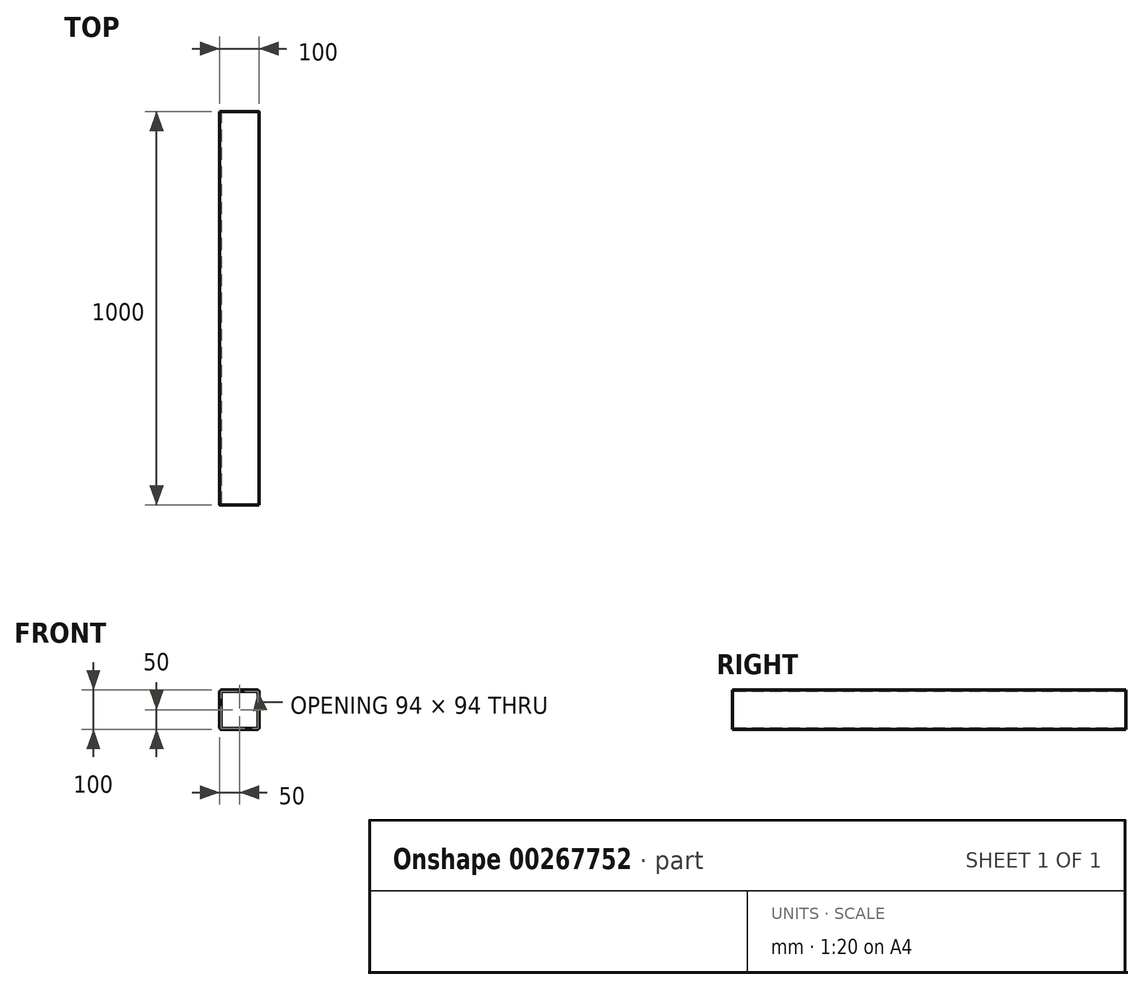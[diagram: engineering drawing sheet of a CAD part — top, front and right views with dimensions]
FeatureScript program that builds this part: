
annotation { "Feature Type Name" : "Feature", "Feature Type Description" : "" }
export const myFeature = defineFeature(function(context is Context, id is Id, definition is map)
    precondition{}
    {
        {
            var Q0;
            Q0=qCreatedBy(makeId("Front.planeOp"),FACE);
            var sketch = newSketch(context, id + "F0", { "sketchPlane" : qUnion([Q0])});
            skLineSegment(sketch, "E0.bottom", {"start": v(45, 50) * mm, "end": v(-45, 50) * mm});
            skLineSegment(sketch, "E0.top", {"start": v(45, -50) * mm, "end": v(-45, -50) * mm});
            skLineSegment(sketch, "E0.left", {"start": v(50, 45) * mm, "end": v(50, -45) * mm});
            skLineSegment(sketch, "E0.right", {"start": v(-50, 45) * mm, "end": v(-50, -45) * mm});
            skPoint(sketch, "E0.middle", {"position": v(0, 0) * mm});
            skPoint(sketch, "E1.visualSharp", {"position": v(-50, 50) * mm});
            skArc(sketch, "E1.filletArc", {"start": v(-45, 50) * mm, "mid": v(-48.54, 48.54) * mm, "end": v(-50, 45) * mm});
            skPoint(sketch, "E2.visualSharp", {"position": v(50, 50) * mm});
            skArc(sketch, "E2.filletArc", {"start": v(50, 45) * mm, "mid": v(48.54, 48.54) * mm, "end": v(45, 50) * mm});
            skPoint(sketch, "E3.visualSharp", {"position": v(50, -50) * mm});
            skArc(sketch, "E3.filletArc", {"start": v(45, -50) * mm, "mid": v(48.54, -48.54) * mm, "end": v(50, -45) * mm});
            skPoint(sketch, "E4.visualSharp", {"position": v(-50, -50) * mm});
            skArc(sketch, "E4.filletArc", {"start": v(-50, -45) * mm, "mid": v(-48.54, -48.54) * mm, "end": v(-45, -50) * mm});
            skArc(sketch, "E5.0", {"start": v(-45, 47) * mm, "mid": v(-46.41, 46.41) * mm, "end": v(-47, 45) * mm});
            skLineSegment(sketch, "E5.1", {"start": v(45, 47) * mm, "end": v(-45, 47) * mm});
            skLineSegment(sketch, "E5.2", {"start": v(-47, 45) * mm, "end": v(-47, -45) * mm});
            skArc(sketch, "E5.3", {"start": v(47, 45) * mm, "mid": v(46.41, 46.41) * mm, "end": v(45, 47) * mm});
            skArc(sketch, "E5.4", {"start": v(-47, -45) * mm, "mid": v(-46.41, -46.41) * mm, "end": v(-45, -47) * mm});
            skLineSegment(sketch, "E5.5", {"start": v(45, -47) * mm, "end": v(-45, -47) * mm});
            skArc(sketch, "E5.6", {"start": v(45, -47) * mm, "mid": v(46.41, -46.41) * mm, "end": v(47, -45) * mm});
            skLineSegment(sketch, "E5.7", {"start": v(47, 45) * mm, "end": v(47, -45) * mm});
            skSolve(sketch);
        }
        {
            var Q0;
            Q0=makeQuery(id+"F0.imprint","IMPRINT",FACE,{"disambiguationData":[TD([[makeQuery(id+"F0.imprint","IMPRINT",EDGE,{"derivedFrom":sQuery(id+"F0.wireOp",EDGE,"E0.bottom")}),1.0]])]});
            extrude(context, id + "F1", {"entities" : qUnion([Q0]), "oppositeDirection" : true, "depth" : 1000 * mm});
        }
    });
